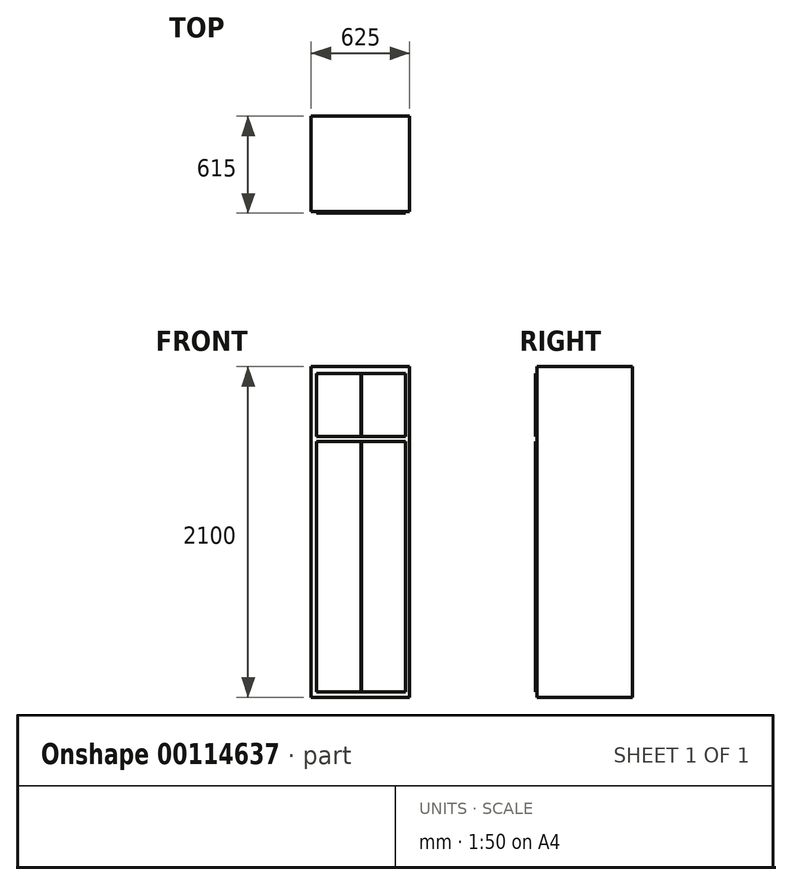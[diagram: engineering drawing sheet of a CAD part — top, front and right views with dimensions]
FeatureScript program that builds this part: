
annotation { "Feature Type Name" : "Feature", "Feature Type Description" : "" }
export const myFeature = defineFeature(function(context is Context, id is Id, definition is map)
    precondition{}
    {
        {
            var Q0;
            Q0=qCreatedBy(makeId("Front.planeOp"),FACE);
            var sketch = newSketch(context, id + "F0", { "sketchPlane" : qUnion([Q0])});
            skLineSegment(sketch, "E0.top", {"start": v(312.5, 1285) * mm, "end": v(-312.5, 1285) * mm});
            skLineSegment(sketch, "E0.left", {"start": v(312.5, -815) * mm, "end": v(312.5, 1285) * mm});
            skLineSegment(sketch, "E0.right", {"start": v(-312.5, -815) * mm, "end": v(-312.5, 1285) * mm});
            skLineSegment(sketch, "E1.left", {"start": v(-312.5, -815) * mm, "end": v(-312.5, -689.53) * mm});
            skLineSegment(sketch, "E1.right", {"start": v(312.5, -815) * mm, "end": v(312.5, -689.53) * mm});
            skLineSegment(sketch, "E2", {"start": v(-312.5, -815) * mm, "end": v(312.5, -815) * mm});
            skSolve(sketch);
        }
        {
            var Q0;
            Q0 = qSketchRegion(id + "F0", true);
            extrude(context, id + "F1", {"entities" : qUnion([Q0]), "depth" : 605 * mm});
        }
        {
            var Q0;
            Q0=makeQuery(id+"F1.opExtrude","CAP_FACE",FACE,{"disambiguationData":[OSD([sQuery(id+"F0.wireOp",EDGE,"E0.top"),sQuery(id+"F0.wireOp",EDGE,"E0.left"),sQuery(id+"F0.wireOp",EDGE,"E0.right"),sQuery(id+"F0.wireOp",EDGE,"E1.left"),sQuery(id+"F0.wireOp",EDGE,"E1.right"),sQuery(id+"F0.wireOp",EDGE,"E2")])],"isStart":false});
            var sketch = newSketch(context, id + "F2", { "sketchPlane" : qUnion([Q0])});
            skPoint(sketch, "E3.middle", {"position": v(94.32, -23.04) * mm});
            skLineSegment(sketch, "E4.bottom", {"start": v(-277.5, 1240) * mm, "end": v(2.5, 1240) * mm});
            skLineSegment(sketch, "E4.top", {"start": v(-277.5, 840) * mm, "end": v(2.5, 840) * mm});
            skLineSegment(sketch, "E4.left", {"start": v(-277.5, 1240) * mm, "end": v(-277.5, 840) * mm});
            skLineSegment(sketch, "E4.right", {"start": v(2.5, 1240) * mm, "end": v(2.5, 840) * mm});
            skLineSegment(sketch, "E5.bottom", {"start": v(7.5, 1240) * mm, "end": v(287.5, 1240) * mm});
            skLineSegment(sketch, "E5.top", {"start": v(7.5, 840) * mm, "end": v(287.5, 840) * mm});
            skLineSegment(sketch, "E5.left", {"start": v(7.5, 1240) * mm, "end": v(7.5, 840) * mm});
            skLineSegment(sketch, "E5.right", {"start": v(287.5, 1240) * mm, "end": v(287.5, 840) * mm});
            skLineSegment(sketch, "E6.bottom", {"start": v(-277.5, 810) * mm, "end": v(2.5, 810) * mm});
            skLineSegment(sketch, "E6.top", {"start": v(-277.5, -780) * mm, "end": v(2.5, -780) * mm});
            skLineSegment(sketch, "E6.left", {"start": v(-277.5, 810) * mm, "end": v(-277.5, -780) * mm});
            skLineSegment(sketch, "E6.right", {"start": v(2.5, 810) * mm, "end": v(2.5, -780) * mm});
            skLineSegment(sketch, "E7.bottom", {"start": v(7.5, 810) * mm, "end": v(287.5, 810) * mm});
            skLineSegment(sketch, "E7.top", {"start": v(7.5, -780) * mm, "end": v(287.5, -780) * mm});
            skLineSegment(sketch, "E7.left", {"start": v(7.5, 810) * mm, "end": v(7.5, -780) * mm});
            skLineSegment(sketch, "E7.right", {"start": v(287.5, 810) * mm, "end": v(287.5, -780) * mm});
            skSolve(sketch);
        }
        {
            var Q0;
            Q0 = qSketchRegion(id + "F2", true);
            extrude(context, id + "F3", {"entities" : qUnion([Q0]), "operationType" : NewBodyOperationType.ADD, "depth" : 10 * mm});
        }
    });
